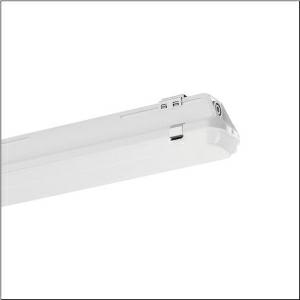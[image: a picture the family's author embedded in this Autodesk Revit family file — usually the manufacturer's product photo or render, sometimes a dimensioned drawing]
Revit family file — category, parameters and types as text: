
# Revit family: monsun_r__21_emergency_51fb107p437c3g_98c5
name_source: partatom
category: Lighting Fixtures
units: mm (PartAtom-declared; Revit-internal decimal feet)

## family parameters
Cut with Voids When Loaded = No
Host = Face
Light Source = No
Part Type = Normal
Room Calculation Point = No
Round Connector Dimension = Use Diameter
Shared = No

## types (1)
- --- (1 x LED, 910 lm, 7.1 W, 4000K)
    Apparent Load = 7 VA
    CIE Flux Codes = 47 77 93 94 100
    Color Rendering = 80
    Color Temperature = 4000K
    Default Elevation = 1800 mm
    Description = Monsun® 21 emergency, damp-proof luminaire, chain hanger, primary optical cover: enclosure, of PMMA, light emission: direct distribution, primary light characteristic: symmetric, installation type: suspended mounting, surface-mounted, horizontal mounting, vertical mounting, LED, rated luminous flux: 3.860lm, luminous efficacy: 175lm/W, light colour: 840, colour temperature: 4000K, control gear: ON/OFF, with terminal, 4-pole, max. 2.5mm², mains connection: 220..240V, AC, 50/60Hz, rated input power: 26W, control gear: single battery element, battery: LiFePO4, 9Ah, housing, of glass-fibre reinforced polyester, uncoated, bright grey, incl. chain hanger, length: 1.590mm, width: 90mm, height: 88mm, clip for enclosure, of stainless steel (V2A), ceiling mounting element, of stainless steel (V2A), chain hanger, of stainless steel (V2A), protection rating (complete): IP66, insulation class (complete): insulation class I (protective earthing), certification: CE, UKCA, protection symbol: D, impact resistance: IK04, permissible operating ambient temperature: +5..+25°C, standard: EN 50419, EN 60598-2-1, EN 60598-2-22, corresponds to IFS (International Featured Standards) requirements for safety and quality in the food industry, for indoor or canopied outdoor use, no direct snow, no direct sun, no direct rain, LABS conformity tested according to VDMA 24364:2018-05, contact your sales advisor before using the luminaires in applications with unclear chemical exposure, large temperature fluctuations or condensation-forming humidity, packaging unit: 1 piece
    Height = 89 mm
    Lamp = 1 x LED
    Lamp Light Flux = 910 lm
    Lamp Power = 7.1 W
    Lamp count = 1
    Length = 1590 mm
    Luminous efficacy = 128 lm/W
    Manufacturer = Siteco
    ModVariant = No
    Model = 51FB107P437C3G
    Mounting Place = Ceiling
    Mounting Type = Surface mounted
    Number of Poles = 1
    OnlyDefault = Yes
    Power Factor = 1
    Product Name = Monsun® 21 emergency
    Product group = damp-proof luminaire
    ProductGroupID = 300
    Protection Class = Protection class I
    Protection Degree = IP 66
    RLX_Detail_Level = 1
    RLX_Emergency_Light_Flux = 0 lm
    RLX_Emergency_Type = 0
    RLX_Emergency_Type_DB = No
    RlxData = <blob elided: 89129 chars, md5=b717db22>
    Socket = socket
    Standby Power = 0 W
    System Light Flux = 910 lm
    System Power = 7 W
    Type Comments = : emergency light operation: 3 h
    Type Image = l_1319656.jpg
    URL = http://relux.com
    VarID = @adj_031774
    Voltage = 0 V
    Weight = 0.00 kg
    Width = 90 mm

## geometry (parser evidence)
native form markers: Blend x4, Sweep x15
no freeform markers — native parametric forms only
